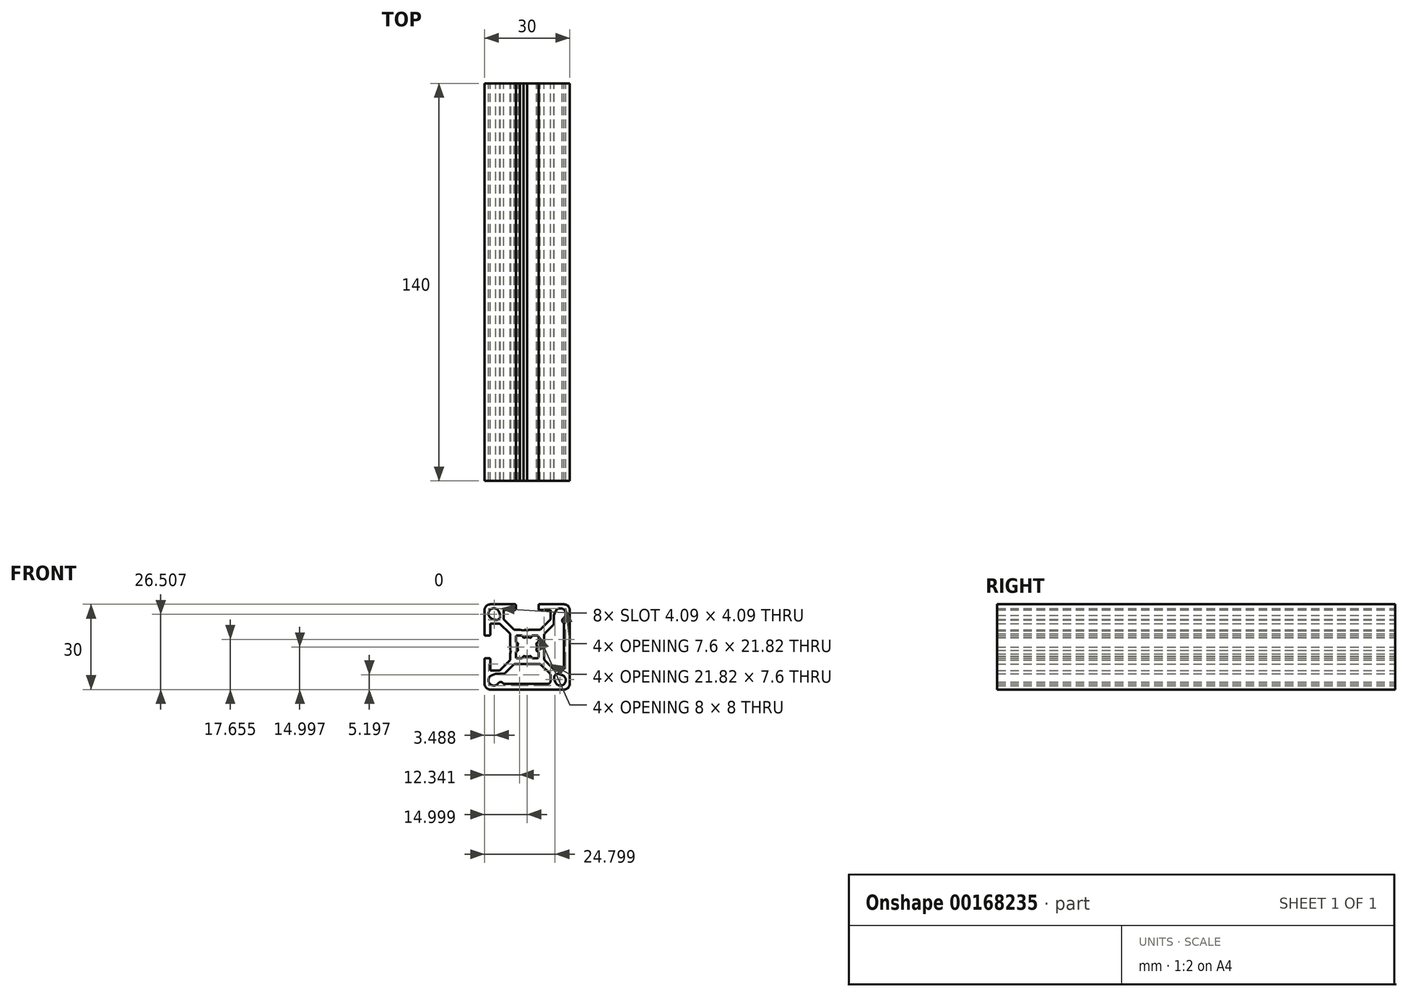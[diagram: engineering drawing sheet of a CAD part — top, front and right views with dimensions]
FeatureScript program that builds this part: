
annotation { "Feature Type Name" : "Feature", "Feature Type Description" : "" }
export const myFeature = defineFeature(function(context is Context, id is Id, definition is map)
    precondition{}
    {
        {
            var Q0;
            Q0=qCreatedBy(makeId("Front.planeOp"),FACE);
            var sketch = newSketch(context, id + "F0", { "sketchPlane" : qUnion([Q0])});
            skLineSegment(sketch, "E0", {"start": v(-39.84, 24.25) * mm, "end": v(-39.84, -9.75) * mm});
            skLineSegment(sketch, "E1", {"start": v(-56.84, 7.25) * mm, "end": v(-22.84, 7.25) * mm});
            skLineSegment(sketch, "E2", {"start": v(-52.84, 22.25) * mm, "end": v(-44.14, 22.25) * mm});
            skLineSegment(sketch, "E3", {"start": v(-52.84, -7.75) * mm, "end": v(-26.84, -7.75) * mm});
            skLineSegment(sketch, "E4", {"start": v(-24.84, 20.25) * mm, "end": v(-24.84, -5.75) * mm});
            skLineSegment(sketch, "E5", {"start": v(-54.84, 20.25) * mm, "end": v(-54.84, 11.55) * mm});
            skArc(sketch, "E6", {"start": v(-24.84, 20.25) * mm, "mid": v(-25.43, 21.66) * mm, "end": v(-26.84, 22.25) * mm});
            skArc(sketch, "E7", {"start": v(-52.84, 22.25) * mm, "mid": v(-54.26, 21.66) * mm, "end": v(-54.84, 20.25) * mm});
            skArc(sketch, "E8", {"start": v(-54.84, -5.75) * mm, "mid": v(-54.26, -7.17) * mm, "end": v(-52.84, -7.75) * mm});
            skArc(sketch, "E9", {"start": v(-26.84, -7.75) * mm, "mid": v(-25.43, -7.17) * mm, "end": v(-24.84, -5.75) * mm});
            skLineSegment(sketch, "E10", {"start": v(-52.84, -1) * mm, "end": v(-52.84, 2.95) * mm});
            skLineSegment(sketch, "E11", {"start": v(-26.84, 15.44) * mm, "end": v(-26.84, 0) * mm});
            skLineSegment(sketch, "E12", {"start": v(-48.03, -5.75) * mm, "end": v(-32.6, -5.75) * mm});
            skLineSegment(sketch, "E13", {"start": v(-54.54, 3.25) * mm, "end": v(-53.14, 3.25) * mm});
            skLineSegment(sketch, "E14", {"start": v(-54.54, 11.25) * mm, "end": v(-53.14, 11.25) * mm});
            skLineSegment(sketch, "E15", {"start": v(-52.84, 11.55) * mm, "end": v(-52.84, 15.5) * mm});
            skLineSegment(sketch, "E16", {"start": v(-35.54, 22.25) * mm, "end": v(-26.84, 22.25) * mm});
            skLineSegment(sketch, "E17", {"start": v(-49.5, -1) * mm, "end": v(-52.84, -1) * mm});
            skLineSegment(sketch, "E18", {"start": v(-49.5, 15.5) * mm, "end": v(-52.84, 15.5) * mm});
            skLineSegment(sketch, "E19", {"start": v(-35.26, 13.25) * mm, "end": v(-39.19, 13.25) * mm});
            skLineSegment(sketch, "E20", {"start": v(-35.67, 1.25) * mm, "end": v(-44.01, 1.25) * mm});
            skLineSegment(sketch, "E21", {"start": v(-33.84, 3.08) * mm, "end": v(-33.84, 11.42) * mm});
            skLineSegment(sketch, "E22", {"start": v(-45.84, 2.66) * mm, "end": v(-45.84, 4.75) * mm});
            skLineSegment(sketch, "E23", {"start": v(-44.43, 13.25) * mm, "end": v(-48.1, 16.91) * mm});
            skLineSegment(sketch, "E24", {"start": v(-45.84, 11.83) * mm, "end": v(-49.5, 15.5) * mm});
            skLineSegment(sketch, "E25", {"start": v(-33.55, 12.13) * mm, "end": v(-30.68, 14.99) * mm});
            skLineSegment(sketch, "E26", {"start": v(-35.26, 13.25) * mm, "end": v(-31.6, 16.91) * mm});
            skLineSegment(sketch, "E27", {"start": v(-33.55, 2.37) * mm, "end": v(-30.47, -0.71) * mm});
            skLineSegment(sketch, "E28", {"start": v(-34.96, 0.95) * mm, "end": v(-31.88, -2.12) * mm});
            skLineSegment(sketch, "E29", {"start": v(-44.72, 0.95) * mm, "end": v(-47.58, -1.91) * mm});
            skLineSegment(sketch, "E30", {"start": v(-45.84, 2.66) * mm, "end": v(-49.5, -1) * mm});
            skLineSegment(sketch, "E31", {"start": v(-54.84, 2.95) * mm, "end": v(-54.84, -5.75) * mm});
            skLineSegment(sketch, "E32", {"start": v(-43.84, 21.95) * mm, "end": v(-43.84, 20.55) * mm});
            skLineSegment(sketch, "E33", {"start": v(-35.84, 21.95) * mm, "end": v(-35.84, 20.55) * mm});
            skLineSegment(sketch, "E34", {"start": v(-31.6, 16.91) * mm, "end": v(-31.6, 20.25) * mm});
            skLineSegment(sketch, "E35", {"start": v(-48.1, 16.91) * mm, "end": v(-48.1, 20.25) * mm});
            skLineSegment(sketch, "E36", {"start": v(-44.14, 20.25) * mm, "end": v(-48.1, 20.25) * mm});
            skLineSegment(sketch, "E37", {"start": v(-35.54, 20.25) * mm, "end": v(-31.6, 20.25) * mm});
            skLineSegment(sketch, "E38", {"start": v(-30.4, 15.7) * mm, "end": v(-30.4, 18.32) * mm});
            skLineSegment(sketch, "E39", {"start": v(-30.4, 18.32) * mm, "end": v(-29.93, 19.6) * mm});
            skArc(sketch, "E40", {"start": v(-27.06, 17.38) * mm, "mid": v(-26.98, 20.45) * mm, "end": v(-29.93, 19.6) * mm});
            skArc(sketch, "E41", {"start": v(-27.06, 17.38) * mm, "mid": v(-27.5, 16.52) * mm, "end": v(-27, 15.7) * mm});
            skArc(sketch, "E42", {"start": v(-26.84, 15.44) * mm, "mid": v(-26.88, 15.59) * mm, "end": v(-27, 15.7) * mm});
            skArc(sketch, "E43", {"start": v(-49.76, 19.6) * mm, "mid": v(-52.88, 20.3) * mm, "end": v(-52.2, 17.16) * mm});
            skLineSegment(sketch, "E44", {"start": v(-49.39, 18.59) * mm, "end": v(-49.76, 19.6) * mm});
            skLineSegment(sketch, "E45", {"start": v(-51.18, 16.8) * mm, "end": v(-52.2, 17.16) * mm});
            skArc(sketch, "E46", {"start": v(-51.18, 16.8) * mm, "mid": v(-49.71, 17.12) * mm, "end": v(-49.39, 18.59) * mm});
            skArc(sketch, "E47", {"start": v(-29.93, -5.1) * mm, "mid": v(-26.8, -5.8) * mm, "end": v(-27.5, -2.67) * mm});
            skLineSegment(sketch, "E48", {"start": v(-28.5, -2.3) * mm, "end": v(-27.5, -2.67) * mm});
            skLineSegment(sketch, "E49", {"start": v(-30.3, -4.1) * mm, "end": v(-29.93, -5.1) * mm});
            skArc(sketch, "E50", {"start": v(-28.5, -2.3) * mm, "mid": v(-29.97, -2.63) * mm, "end": v(-30.3, -4.1) * mm});
            skArc(sketch, "E51", {"start": v(-33.55, 12.13) * mm, "mid": v(-33.76, 11.8) * mm, "end": v(-33.84, 11.42) * mm});
            skArc(sketch, "E52", {"start": v(-33.84, 3.08) * mm, "mid": v(-33.76, 2.7) * mm, "end": v(-33.55, 2.37) * mm});
            skLineSegment(sketch, "E53", {"start": v(-29.76, -1) * mm, "end": v(-27.84, -1) * mm});
            skArc(sketch, "E54", {"start": v(-30.47, -0.71) * mm, "mid": v(-30.15, -0.93) * mm, "end": v(-29.76, -1) * mm});
            skArc(sketch, "E55", {"start": v(-27.84, -1) * mm, "mid": v(-27.13, -0.71) * mm, "end": v(-26.84, 0) * mm});
            skArc(sketch, "E56", {"start": v(-30.68, 14.99) * mm, "mid": v(-30.47, 15.31) * mm, "end": v(-30.4, 15.7) * mm});
            skLineSegment(sketch, "E57", {"start": v(-31.6, -2.83) * mm, "end": v(-31.6, -4.75) * mm});
            skLineSegment(sketch, "E58", {"start": v(-48.3, -2.2) * mm, "end": v(-50.91, -2.2) * mm});
            skLineSegment(sketch, "E59", {"start": v(-50.91, -2.2) * mm, "end": v(-52.2, -2.67) * mm});
            skArc(sketch, "E60", {"start": v(-52.2, -2.67) * mm, "mid": v(-53.04, -5.61) * mm, "end": v(-49.98, -5.53) * mm});
            skArc(sketch, "E61", {"start": v(-48.29, -5.6) * mm, "mid": v(-49.12, -5.1) * mm, "end": v(-49.98, -5.53) * mm});
            skArc(sketch, "E62", {"start": v(-48.29, -5.6) * mm, "mid": v(-48.18, -5.71) * mm, "end": v(-48.03, -5.75) * mm});
            skArc(sketch, "E63", {"start": v(-48.3, -2.2) * mm, "mid": v(-47.9, -2.13) * mm, "end": v(-47.58, -1.91) * mm});
            skArc(sketch, "E64", {"start": v(-44.01, 1.25) * mm, "mid": v(-44.4, 1.17) * mm, "end": v(-44.72, 0.95) * mm});
            skArc(sketch, "E65", {"start": v(-34.96, 0.95) * mm, "mid": v(-35.29, 1.17) * mm, "end": v(-35.67, 1.25) * mm});
            skArc(sketch, "E66", {"start": v(-31.6, -2.83) * mm, "mid": v(-31.67, -2.45) * mm, "end": v(-31.88, -2.12) * mm});
            skArc(sketch, "E67", {"start": v(-32.6, -5.75) * mm, "mid": v(-31.88, -5.46) * mm, "end": v(-31.6, -4.75) * mm});
            skLineSegment(sketch, "E68", {"start": v(-36.34, 11.25) * mm, "end": v(-37.85, 11.25) * mm});
            skLineSegment(sketch, "E69", {"start": v(-35.84, 3.75) * mm, "end": v(-35.84, 5.25) * mm});
            skLineSegment(sketch, "E70", {"start": v(-36.34, 3.25) * mm, "end": v(-37.85, 3.25) * mm});
            skLineSegment(sketch, "E71", {"start": v(-43.84, 3.75) * mm, "end": v(-43.84, 5.25) * mm});
            skLineSegment(sketch, "E72", {"start": v(-42.34, 13.25) * mm, "end": v(-41.06, 13) * mm});
            skLineSegment(sketch, "E73", {"start": v(-39.84, 12.95) * mm, "end": v(-40.24, 13.18) * mm});
            skLineSegment(sketch, "E74", {"start": v(-39.84, 12.95) * mm, "end": v(-39.44, 13.18) * mm});
            skLineSegment(sketch, "E75", {"start": v(-42.34, 13.25) * mm, "end": v(-44.43, 13.25) * mm});
            skArc(sketch, "E76", {"start": v(-39.19, 13.25) * mm, "mid": v(-39.32, 13.23) * mm, "end": v(-39.44, 13.18) * mm});
            skArc(sketch, "E77", {"start": v(-40.24, 13.18) * mm, "mid": v(-40.5, 13.25) * mm, "end": v(-40.74, 13.18) * mm});
            skLineSegment(sketch, "E78", {"start": v(-41.06, 13) * mm, "end": v(-40.74, 13.18) * mm});
            skArc(sketch, "E79", {"start": v(-45.84, 7.9) * mm, "mid": v(-45.82, 7.77) * mm, "end": v(-45.77, 7.65) * mm});
            skLineSegment(sketch, "E80", {"start": v(-45.84, 4.75) * mm, "end": v(-45.6, 6.03) * mm});
            skLineSegment(sketch, "E81", {"start": v(-45.54, 7.25) * mm, "end": v(-45.77, 6.84) * mm});
            skLineSegment(sketch, "E82", {"start": v(-45.54, 7.25) * mm, "end": v(-45.77, 7.65) * mm});
            skArc(sketch, "E83", {"start": v(-45.77, 6.84) * mm, "mid": v(-45.84, 6.6) * mm, "end": v(-45.77, 6.34) * mm});
            skLineSegment(sketch, "E84", {"start": v(-45.6, 6.03) * mm, "end": v(-45.77, 6.34) * mm});
            skLineSegment(sketch, "E85", {"start": v(-45.84, 7.9) * mm, "end": v(-45.84, 11.83) * mm});
            skArc(sketch, "E86", {"start": v(-35.84, 20.55) * mm, "mid": v(-35.75, 20.33) * mm, "end": v(-35.54, 20.25) * mm});
            skArc(sketch, "E87", {"start": v(-35.54, 22.25) * mm, "mid": v(-35.75, 22.16) * mm, "end": v(-35.84, 21.95) * mm});
            skArc(sketch, "E88", {"start": v(-44.14, 20.25) * mm, "mid": v(-43.93, 20.33) * mm, "end": v(-43.84, 20.55) * mm});
            skArc(sketch, "E89", {"start": v(-43.84, 21.95) * mm, "mid": v(-43.93, 22.16) * mm, "end": v(-44.14, 22.25) * mm});
            skArc(sketch, "E90", {"start": v(-53.14, 11.25) * mm, "mid": v(-52.93, 11.33) * mm, "end": v(-52.84, 11.55) * mm});
            skArc(sketch, "E91", {"start": v(-54.84, 11.55) * mm, "mid": v(-54.75, 11.33) * mm, "end": v(-54.54, 11.25) * mm});
            skArc(sketch, "E92", {"start": v(-52.84, 2.95) * mm, "mid": v(-52.93, 3.16) * mm, "end": v(-53.14, 3.25) * mm});
            skArc(sketch, "E93", {"start": v(-54.54, 3.25) * mm, "mid": v(-54.75, 3.16) * mm, "end": v(-54.84, 2.95) * mm});
            skArc(sketch, "E94", {"start": v(-38.85, 10.5) * mm, "mid": v(-39.84, 10.65) * mm, "end": v(-40.83, 10.5) * mm});
            skArc(sketch, "E95", {"start": v(-41.34, 10.82) * mm, "mid": v(-41.16, 10.54) * mm, "end": v(-40.83, 10.5) * mm});
            skArc(sketch, "E96", {"start": v(-41.34, 10.82) * mm, "mid": v(-41.5, 11.13) * mm, "end": v(-41.84, 11.25) * mm});
            skArc(sketch, "E97", {"start": v(-38.85, 10.5) * mm, "mid": v(-38.52, 10.54) * mm, "end": v(-38.34, 10.82) * mm});
            skArc(sketch, "E98", {"start": v(-37.85, 11.25) * mm, "mid": v(-38.17, 11.13) * mm, "end": v(-38.34, 10.82) * mm});
            skLineSegment(sketch, "E99", {"start": v(-41.84, 11.25) * mm, "end": v(-43.34, 11.25) * mm});
            skArc(sketch, "E100", {"start": v(-43.34, 11.25) * mm, "mid": v(-43.7, 11.1) * mm, "end": v(-43.84, 10.75) * mm});
            skArc(sketch, "E101", {"start": v(-35.84, 10.75) * mm, "mid": v(-35.99, 11.1) * mm, "end": v(-36.34, 11.25) * mm});
            skArc(sketch, "E102", {"start": v(-36.34, 3.25) * mm, "mid": v(-35.99, 3.4) * mm, "end": v(-35.84, 3.75) * mm});
            skArc(sketch, "E103", {"start": v(-43.84, 3.75) * mm, "mid": v(-43.7, 3.4) * mm, "end": v(-43.34, 3.25) * mm});
            skArc(sketch, "E104", {"start": v(-43.1, 8.23) * mm, "mid": v(-43.24, 7.25) * mm, "end": v(-43.1, 6.26) * mm});
            skArc(sketch, "E105", {"start": v(-43.42, 5.75) * mm, "mid": v(-43.14, 5.93) * mm, "end": v(-43.1, 6.26) * mm});
            skArc(sketch, "E106", {"start": v(-43.42, 5.75) * mm, "mid": v(-43.72, 5.58) * mm, "end": v(-43.84, 5.25) * mm});
            skArc(sketch, "E107", {"start": v(-43.1, 8.23) * mm, "mid": v(-43.14, 8.56) * mm, "end": v(-43.42, 8.75) * mm});
            skArc(sketch, "E108", {"start": v(-43.84, 9.24) * mm, "mid": v(-43.72, 8.92) * mm, "end": v(-43.42, 8.75) * mm});
            skArc(sketch, "E109", {"start": v(-36.59, 6.26) * mm, "mid": v(-36.44, 7.25) * mm, "end": v(-36.59, 8.23) * mm});
            skArc(sketch, "E110", {"start": v(-36.27, 8.75) * mm, "mid": v(-36.54, 8.56) * mm, "end": v(-36.59, 8.23) * mm});
            skArc(sketch, "E111", {"start": v(-36.27, 8.75) * mm, "mid": v(-35.96, 8.92) * mm, "end": v(-35.84, 9.24) * mm});
            skArc(sketch, "E112", {"start": v(-36.59, 6.26) * mm, "mid": v(-36.54, 5.93) * mm, "end": v(-36.27, 5.75) * mm});
            skArc(sketch, "E113", {"start": v(-35.84, 5.25) * mm, "mid": v(-35.96, 5.58) * mm, "end": v(-36.27, 5.75) * mm});
            skArc(sketch, "E114", {"start": v(-40.83, 4) * mm, "mid": v(-39.84, 3.85) * mm, "end": v(-38.85, 4) * mm});
            skArc(sketch, "E115", {"start": v(-40.83, 4) * mm, "mid": v(-41.16, 3.95) * mm, "end": v(-41.34, 3.67) * mm});
            skArc(sketch, "E116", {"start": v(-41.84, 3.25) * mm, "mid": v(-41.5, 3.37) * mm, "end": v(-41.34, 3.67) * mm});
            skArc(sketch, "E117", {"start": v(-38.34, 3.67) * mm, "mid": v(-38.52, 3.95) * mm, "end": v(-38.85, 4) * mm});
            skArc(sketch, "E118", {"start": v(-38.34, 3.67) * mm, "mid": v(-38.17, 3.37) * mm, "end": v(-37.85, 3.25) * mm});
            skLineSegment(sketch, "E119", {"start": v(-35.84, 9.24) * mm, "end": v(-35.84, 10.75) * mm});
            skLineSegment(sketch, "E120", {"start": v(-41.84, 3.25) * mm, "end": v(-43.34, 3.25) * mm});
            skLineSegment(sketch, "E121", {"start": v(-43.84, 9.24) * mm, "end": v(-43.84, 10.75) * mm});
            skCircle(sketch, "E122", {"center": v(-39.84, 7.25) * mm, "radius": 3.4 * mm});
            skLineSegment(sketch, "E123", {"start": v(-28.14, 22.85) * mm, "end": v(-28.14, 15.05) * mm});
            skLineSegment(sketch, "E124", {"start": v(-32.04, 18.95) * mm, "end": v(-24.24, 18.95) * mm});
            skLineSegment(sketch, "E125", {"start": v(-28.14, -0.55) * mm, "end": v(-28.14, -8.35) * mm});
            skLineSegment(sketch, "E126", {"start": v(-32.04, -4.45) * mm, "end": v(-24.24, -4.45) * mm});
            skLineSegment(sketch, "E127", {"start": v(-51.54, -0.55) * mm, "end": v(-51.54, -8.35) * mm});
            skLineSegment(sketch, "E128", {"start": v(-55.44, -4.45) * mm, "end": v(-47.64, -4.45) * mm});
            skLineSegment(sketch, "E129", {"start": v(-51.54, 22.85) * mm, "end": v(-51.54, 15.05) * mm});
            skLineSegment(sketch, "E130", {"start": v(-55.44, 18.95) * mm, "end": v(-47.64, 18.95) * mm});
            skSolve(sketch);
        }
        {
            var Q0;
            Q0=qCreatedBy(makeId("Front.planeOp"),FACE);
            var sketch = newSketch(context, id + "F1", { "sketchPlane" : qUnion([Q0])});
            skArc(sketch, "E131.0", {"start": v(-48.29, -5.6) * mm, "mid": v(-49.12, -5.1) * mm, "end": v(-49.98, -5.53) * mm});
            skLineSegment(sketch, "E131.1", {"start": v(-44.72, 0.95) * mm, "end": v(-47.58, -1.91) * mm});
            skLineSegment(sketch, "E131.3", {"start": v(-35.67, 1.25) * mm, "end": v(-44.01, 1.25) * mm});
            skLineSegment(sketch, "E131.4", {"start": v(-44.14, 20.25) * mm, "end": v(-48.1, 20.25) * mm});
            skArc(sketch, "E131.5", {"start": v(-51.18, 16.8) * mm, "mid": v(-49.71, 17.12) * mm, "end": v(-49.39, 18.59) * mm});
            skLineSegment(sketch, "E131.6", {"start": v(-45.84, 2.66) * mm, "end": v(-49.5, -1) * mm});
            skLineSegment(sketch, "E131.7", {"start": v(-33.84, 3.08) * mm, "end": v(-33.84, 11.42) * mm});
            skLineSegment(sketch, "E131.8", {"start": v(-45.84, 7.9) * mm, "end": v(-45.84, 11.83) * mm});
            skLineSegment(sketch, "E131.9", {"start": v(-35.54, 20.25) * mm, "end": v(-31.6, 20.25) * mm});
            skLineSegment(sketch, "E131.10", {"start": v(-45.84, 2.66) * mm, "end": v(-45.84, 4.75) * mm});
            skLineSegment(sketch, "E131.11", {"start": v(-30.4, 15.7) * mm, "end": v(-30.4, 18.32) * mm});
            skLineSegment(sketch, "E131.12", {"start": v(-44.43, 13.25) * mm, "end": v(-48.1, 16.91) * mm});
            skLineSegment(sketch, "E131.13", {"start": v(-48.1, 16.91) * mm, "end": v(-48.1, 20.25) * mm});
            skLineSegment(sketch, "E131.15", {"start": v(-31.6, 16.91) * mm, "end": v(-31.6, 20.25) * mm});
            skArc(sketch, "E131.16", {"start": v(-28.5, -2.3) * mm, "mid": v(-29.97, -2.63) * mm, "end": v(-30.3, -4.1) * mm});
            skLineSegment(sketch, "E131.17", {"start": v(-49.5, 15.5) * mm, "end": v(-52.84, 15.5) * mm});
            skLineSegment(sketch, "E131.18", {"start": v(-35.26, 13.25) * mm, "end": v(-39.19, 13.25) * mm});
            skLineSegment(sketch, "E131.19", {"start": v(-48.03, -5.75) * mm, "end": v(-32.6, -5.75) * mm});
            skLineSegment(sketch, "E131.20", {"start": v(-26.84, 15.44) * mm, "end": v(-26.84, 0) * mm});
            skLineSegment(sketch, "E131.21", {"start": v(-52.84, -1) * mm, "end": v(-52.84, 2.95) * mm});
            skArc(sketch, "E131.23", {"start": v(-26.84, -7.75) * mm, "mid": v(-25.43, -7.17) * mm, "end": v(-24.84, -5.75) * mm});
            skArc(sketch, "E131.24", {"start": v(-54.84, -5.75) * mm, "mid": v(-54.26, -7.17) * mm, "end": v(-52.84, -7.75) * mm});
            skArc(sketch, "E131.25", {"start": v(-52.84, 22.25) * mm, "mid": v(-54.26, 21.66) * mm, "end": v(-54.84, 20.25) * mm});
            skArc(sketch, "E131.26", {"start": v(-24.84, 20.25) * mm, "mid": v(-25.43, 21.66) * mm, "end": v(-26.84, 22.25) * mm});
            skLineSegment(sketch, "E131.27", {"start": v(-54.84, 20.25) * mm, "end": v(-54.84, 11.55) * mm});
            skLineSegment(sketch, "E131.28", {"start": v(-24.84, 20.25) * mm, "end": v(-24.84, -5.75) * mm});
            skLineSegment(sketch, "E131.29", {"start": v(-49.5, -1) * mm, "end": v(-52.84, -1) * mm});
            skLineSegment(sketch, "E131.30", {"start": v(-52.84, -7.75) * mm, "end": v(-26.84, -7.75) * mm});
            skLineSegment(sketch, "E131.31", {"start": v(-52.84, 22.25) * mm, "end": v(-44.14, 22.25) * mm});
            skLineSegment(sketch, "E131.32", {"start": v(-52.84, 11.55) * mm, "end": v(-52.84, 15.5) * mm});
            skLineSegment(sketch, "E131.33", {"start": v(-34.96, 0.95) * mm, "end": v(-31.88, -2.12) * mm});
            skArc(sketch, "E131.34", {"start": v(-52.2, -2.67) * mm, "mid": v(-53.04, -5.61) * mm, "end": v(-49.98, -5.53) * mm});
            skLineSegment(sketch, "E131.35", {"start": v(-42.34, 13.25) * mm, "end": v(-44.43, 13.25) * mm});
            skLineSegment(sketch, "E131.37", {"start": v(-33.55, 2.37) * mm, "end": v(-30.47, -0.71) * mm});
            skArc(sketch, "E131.38", {"start": v(-49.76, 19.6) * mm, "mid": v(-52.88, 20.3) * mm, "end": v(-52.2, 17.16) * mm});
            skLineSegment(sketch, "E131.39", {"start": v(-35.54, 22.25) * mm, "end": v(-26.84, 22.25) * mm});
            skLineSegment(sketch, "E131.41", {"start": v(-35.26, 13.25) * mm, "end": v(-31.6, 16.91) * mm});
            skLineSegment(sketch, "E131.42", {"start": v(-48.3, -2.2) * mm, "end": v(-50.91, -2.2) * mm});
            skLineSegment(sketch, "E131.43", {"start": v(-33.55, 12.13) * mm, "end": v(-30.68, 14.99) * mm});
            skLineSegment(sketch, "E131.46", {"start": v(-54.84, 2.95) * mm, "end": v(-54.84, -5.75) * mm});
            skArc(sketch, "E131.47", {"start": v(-29.93, -5.1) * mm, "mid": v(-26.8, -5.8) * mm, "end": v(-27.5, -2.67) * mm});
            skLineSegment(sketch, "E131.48", {"start": v(-45.84, 11.83) * mm, "end": v(-49.5, 15.5) * mm});
            skArc(sketch, "E131.49", {"start": v(-27.06, 17.38) * mm, "mid": v(-26.98, 20.45) * mm, "end": v(-29.93, 19.6) * mm});
            skArc(sketch, "E131.50", {"start": v(-36.59, 6.26) * mm, "mid": v(-36.44, 7.25) * mm, "end": v(-36.59, 8.23) * mm});
            skArc(sketch, "E131.51", {"start": v(-38.85, 10.5) * mm, "mid": v(-39.84, 10.65) * mm, "end": v(-40.83, 10.5) * mm});
            skArc(sketch, "E131.52", {"start": v(-40.83, 4) * mm, "mid": v(-39.84, 3.85) * mm, "end": v(-38.85, 4) * mm});
            skLineSegment(sketch, "E131.53", {"start": v(-31.6, -2.83) * mm, "end": v(-31.6, -4.75) * mm});
            skArc(sketch, "E131.54", {"start": v(-43.1, 8.23) * mm, "mid": v(-43.24, 7.25) * mm, "end": v(-43.1, 6.26) * mm});
            skArc(sketch, "E131.55", {"start": v(-40.83, 4) * mm, "mid": v(-41.16, 3.95) * mm, "end": v(-41.34, 3.67) * mm});
            skLineSegment(sketch, "E131.56", {"start": v(-51.18, 16.8) * mm, "end": v(-52.2, 17.16) * mm});
            skLineSegment(sketch, "E131.57", {"start": v(-41.84, 11.25) * mm, "end": v(-43.34, 11.25) * mm});
            skLineSegment(sketch, "E131.58", {"start": v(-36.34, 11.25) * mm, "end": v(-37.85, 11.25) * mm});
            skArc(sketch, "E131.59", {"start": v(-33.84, 3.08) * mm, "mid": v(-33.76, 2.7) * mm, "end": v(-33.55, 2.37) * mm});
            skArc(sketch, "E131.60", {"start": v(-41.84, 3.25) * mm, "mid": v(-41.5, 3.37) * mm, "end": v(-41.34, 3.67) * mm});
            skArc(sketch, "E131.61", {"start": v(-43.34, 11.25) * mm, "mid": v(-43.7, 11.1) * mm, "end": v(-43.84, 10.75) * mm});
            skArc(sketch, "E131.62", {"start": v(-36.27, 8.75) * mm, "mid": v(-36.54, 8.56) * mm, "end": v(-36.59, 8.23) * mm});
            skLineSegment(sketch, "E131.63", {"start": v(-35.84, 3.75) * mm, "end": v(-35.84, 5.25) * mm});
            skLineSegment(sketch, "E131.64", {"start": v(-29.76, -1) * mm, "end": v(-27.84, -1) * mm});
            skArc(sketch, "E131.65", {"start": v(-38.34, 3.67) * mm, "mid": v(-38.52, 3.95) * mm, "end": v(-38.85, 4) * mm});
            skArc(sketch, "E131.66", {"start": v(-35.84, 10.75) * mm, "mid": v(-35.99, 11.1) * mm, "end": v(-36.34, 11.25) * mm});
            skArc(sketch, "E131.67", {"start": v(-35.84, 20.55) * mm, "mid": v(-35.75, 20.33) * mm, "end": v(-35.54, 20.25) * mm});
            skLineSegment(sketch, "E131.68", {"start": v(-36.34, 3.25) * mm, "end": v(-37.85, 3.25) * mm});
            skArc(sketch, "E131.69", {"start": v(-30.47, -0.71) * mm, "mid": v(-30.15, -0.93) * mm, "end": v(-29.76, -1) * mm});
            skArc(sketch, "E131.70", {"start": v(-38.34, 3.67) * mm, "mid": v(-38.17, 3.37) * mm, "end": v(-37.85, 3.25) * mm});
            skArc(sketch, "E131.71", {"start": v(-36.34, 3.25) * mm, "mid": v(-35.99, 3.4) * mm, "end": v(-35.84, 3.75) * mm});
            skArc(sketch, "E131.72", {"start": v(-27.84, -1) * mm, "mid": v(-27.13, -0.71) * mm, "end": v(-26.84, 0) * mm});
            skLineSegment(sketch, "E131.73", {"start": v(-30.4, 18.32) * mm, "end": v(-29.93, 19.6) * mm});
            skLineSegment(sketch, "E131.74", {"start": v(-35.84, 9.24) * mm, "end": v(-35.84, 10.75) * mm});
            skArc(sketch, "E131.75", {"start": v(-43.84, 3.75) * mm, "mid": v(-43.7, 3.4) * mm, "end": v(-43.34, 3.25) * mm});
            skArc(sketch, "E131.76", {"start": v(-35.54, 22.25) * mm, "mid": v(-35.75, 22.16) * mm, "end": v(-35.84, 21.95) * mm});
            skLineSegment(sketch, "E131.77", {"start": v(-43.84, 3.75) * mm, "end": v(-43.84, 5.25) * mm});
            skArc(sketch, "E131.78", {"start": v(-31.6, -2.83) * mm, "mid": v(-31.67, -2.45) * mm, "end": v(-31.88, -2.12) * mm});
            skArc(sketch, "E131.79", {"start": v(-48.3, -2.2) * mm, "mid": v(-47.9, -2.13) * mm, "end": v(-47.58, -1.91) * mm});
            skArc(sketch, "E131.80", {"start": v(-33.55, 12.13) * mm, "mid": v(-33.76, 11.8) * mm, "end": v(-33.84, 11.42) * mm});
            skArc(sketch, "E131.81", {"start": v(-32.6, -5.75) * mm, "mid": v(-31.88, -5.46) * mm, "end": v(-31.6, -4.75) * mm});
            skLineSegment(sketch, "E131.82", {"start": v(-35.84, 21.95) * mm, "end": v(-35.84, 20.55) * mm});
            skLineSegment(sketch, "E131.83", {"start": v(-30.3, -4.1) * mm, "end": v(-29.93, -5.1) * mm});
            skArc(sketch, "E131.84", {"start": v(-34.96, 0.95) * mm, "mid": v(-35.29, 1.17) * mm, "end": v(-35.67, 1.25) * mm});
            skArc(sketch, "E131.85", {"start": v(-39.19, 13.25) * mm, "mid": v(-39.32, 13.23) * mm, "end": v(-39.44, 13.18) * mm});
            skArc(sketch, "E131.86", {"start": v(-43.84, 9.24) * mm, "mid": v(-43.72, 8.92) * mm, "end": v(-43.42, 8.75) * mm});
            skLineSegment(sketch, "E131.87", {"start": v(-49.39, 18.59) * mm, "end": v(-49.76, 19.6) * mm});
            skArc(sketch, "E131.88", {"start": v(-43.1, 8.23) * mm, "mid": v(-43.14, 8.56) * mm, "end": v(-43.42, 8.75) * mm});
            skLineSegment(sketch, "E131.89", {"start": v(-50.91, -2.2) * mm, "end": v(-52.2, -2.67) * mm});
            skLineSegment(sketch, "E131.90", {"start": v(-28.5, -2.3) * mm, "end": v(-27.5, -2.67) * mm});
            skArc(sketch, "E131.91", {"start": v(-44.01, 1.25) * mm, "mid": v(-44.4, 1.17) * mm, "end": v(-44.72, 0.95) * mm});
            skLineSegment(sketch, "E131.92", {"start": v(-45.84, 4.75) * mm, "end": v(-45.6, 6.03) * mm});
            skArc(sketch, "E131.93", {"start": v(-26.84, 15.44) * mm, "mid": v(-26.88, 15.59) * mm, "end": v(-27, 15.7) * mm});
            skLineSegment(sketch, "E131.94", {"start": v(-43.84, 9.24) * mm, "end": v(-43.84, 10.75) * mm});
            skArc(sketch, "E131.95", {"start": v(-27.06, 17.38) * mm, "mid": v(-27.5, 16.52) * mm, "end": v(-27, 15.7) * mm});
            skArc(sketch, "E131.96", {"start": v(-36.27, 8.75) * mm, "mid": v(-35.96, 8.92) * mm, "end": v(-35.84, 9.24) * mm});
            skLineSegment(sketch, "E131.97", {"start": v(-42.34, 13.25) * mm, "end": v(-41.06, 13) * mm});
            skLineSegment(sketch, "E131.98", {"start": v(-41.84, 3.25) * mm, "end": v(-43.34, 3.25) * mm});
            skArc(sketch, "E131.99", {"start": v(-30.68, 14.99) * mm, "mid": v(-30.47, 15.31) * mm, "end": v(-30.4, 15.7) * mm});
            skArc(sketch, "E131.100", {"start": v(-40.24, 13.18) * mm, "mid": v(-40.5, 13.25) * mm, "end": v(-40.74, 13.18) * mm});
            skLineSegment(sketch, "E131.101", {"start": v(-45.6, 6.03) * mm, "end": v(-45.77, 6.34) * mm});
            skLineSegment(sketch, "E131.102", {"start": v(-41.06, 13) * mm, "end": v(-40.74, 13.18) * mm});
            skArc(sketch, "E131.103", {"start": v(-48.29, -5.6) * mm, "mid": v(-48.18, -5.71) * mm, "end": v(-48.03, -5.75) * mm});
            skArc(sketch, "E131.104", {"start": v(-37.85, 11.25) * mm, "mid": v(-38.17, 11.13) * mm, "end": v(-38.34, 10.82) * mm});
            skArc(sketch, "E131.105", {"start": v(-38.85, 10.5) * mm, "mid": v(-38.52, 10.54) * mm, "end": v(-38.34, 10.82) * mm});
            skArc(sketch, "E131.106", {"start": v(-35.84, 5.25) * mm, "mid": v(-35.96, 5.58) * mm, "end": v(-36.27, 5.75) * mm});
            skLineSegment(sketch, "E131.107", {"start": v(-54.54, 11.25) * mm, "end": v(-53.14, 11.25) * mm});
            skArc(sketch, "E131.108", {"start": v(-54.84, 11.55) * mm, "mid": v(-54.75, 11.33) * mm, "end": v(-54.54, 11.25) * mm});
            skLineSegment(sketch, "E131.109", {"start": v(-39.84, 12.95) * mm, "end": v(-39.44, 13.18) * mm});
            skArc(sketch, "E131.110", {"start": v(-53.14, 11.25) * mm, "mid": v(-52.93, 11.33) * mm, "end": v(-52.84, 11.55) * mm});
            skArc(sketch, "E131.111", {"start": v(-43.42, 5.75) * mm, "mid": v(-43.72, 5.58) * mm, "end": v(-43.84, 5.25) * mm});
            skArc(sketch, "E131.112", {"start": v(-41.34, 10.82) * mm, "mid": v(-41.5, 11.13) * mm, "end": v(-41.84, 11.25) * mm});
            skLineSegment(sketch, "E131.113", {"start": v(-39.84, 12.95) * mm, "end": v(-40.24, 13.18) * mm});
            skArc(sketch, "E131.114", {"start": v(-43.42, 5.75) * mm, "mid": v(-43.14, 5.93) * mm, "end": v(-43.1, 6.26) * mm});
            skArc(sketch, "E131.115", {"start": v(-36.59, 6.26) * mm, "mid": v(-36.54, 5.93) * mm, "end": v(-36.27, 5.75) * mm});
            skArc(sketch, "E131.116", {"start": v(-41.34, 10.82) * mm, "mid": v(-41.16, 10.54) * mm, "end": v(-40.83, 10.5) * mm});
            skLineSegment(sketch, "E131.117", {"start": v(-45.54, 7.25) * mm, "end": v(-45.77, 7.65) * mm});
            skArc(sketch, "E131.118", {"start": v(-45.77, 6.84) * mm, "mid": v(-45.84, 6.6) * mm, "end": v(-45.77, 6.34) * mm});
            skLineSegment(sketch, "E131.119", {"start": v(-43.84, 21.95) * mm, "end": v(-43.84, 20.55) * mm});
            skArc(sketch, "E131.120", {"start": v(-43.84, 21.95) * mm, "mid": v(-43.93, 22.16) * mm, "end": v(-44.14, 22.25) * mm});
            skArc(sketch, "E131.121", {"start": v(-44.14, 20.25) * mm, "mid": v(-43.93, 20.33) * mm, "end": v(-43.84, 20.55) * mm});
            skArc(sketch, "E131.122", {"start": v(-54.54, 3.25) * mm, "mid": v(-54.75, 3.16) * mm, "end": v(-54.84, 2.95) * mm});
            skArc(sketch, "E131.123", {"start": v(-45.84, 7.9) * mm, "mid": v(-45.82, 7.77) * mm, "end": v(-45.77, 7.65) * mm});
            skLineSegment(sketch, "E131.124", {"start": v(-45.54, 7.25) * mm, "end": v(-45.77, 6.84) * mm});
            skLineSegment(sketch, "E131.125", {"start": v(-54.54, 3.25) * mm, "end": v(-53.14, 3.25) * mm});
            skArc(sketch, "E131.126", {"start": v(-52.84, 2.95) * mm, "mid": v(-52.93, 3.16) * mm, "end": v(-53.14, 3.25) * mm});
            skSolve(sketch);
        }
        {
            var Q0;
            Q0=makeQuery(id+"F1.imprint","IMPRINT",FACE,{"disambiguationData":[TD([[makeQuery(id+"F1.imprint","IMPRINT",EDGE,{"derivedFrom":sQuery(id+"F1.wireOp",EDGE,"E131.0")}),1.0]])]});
            extrude(context, id + "F2", {"entities" : qUnion([Q0]), "endBound" : BoundingType.SYMMETRIC, "depth" : 140 * mm});
        }
    });
